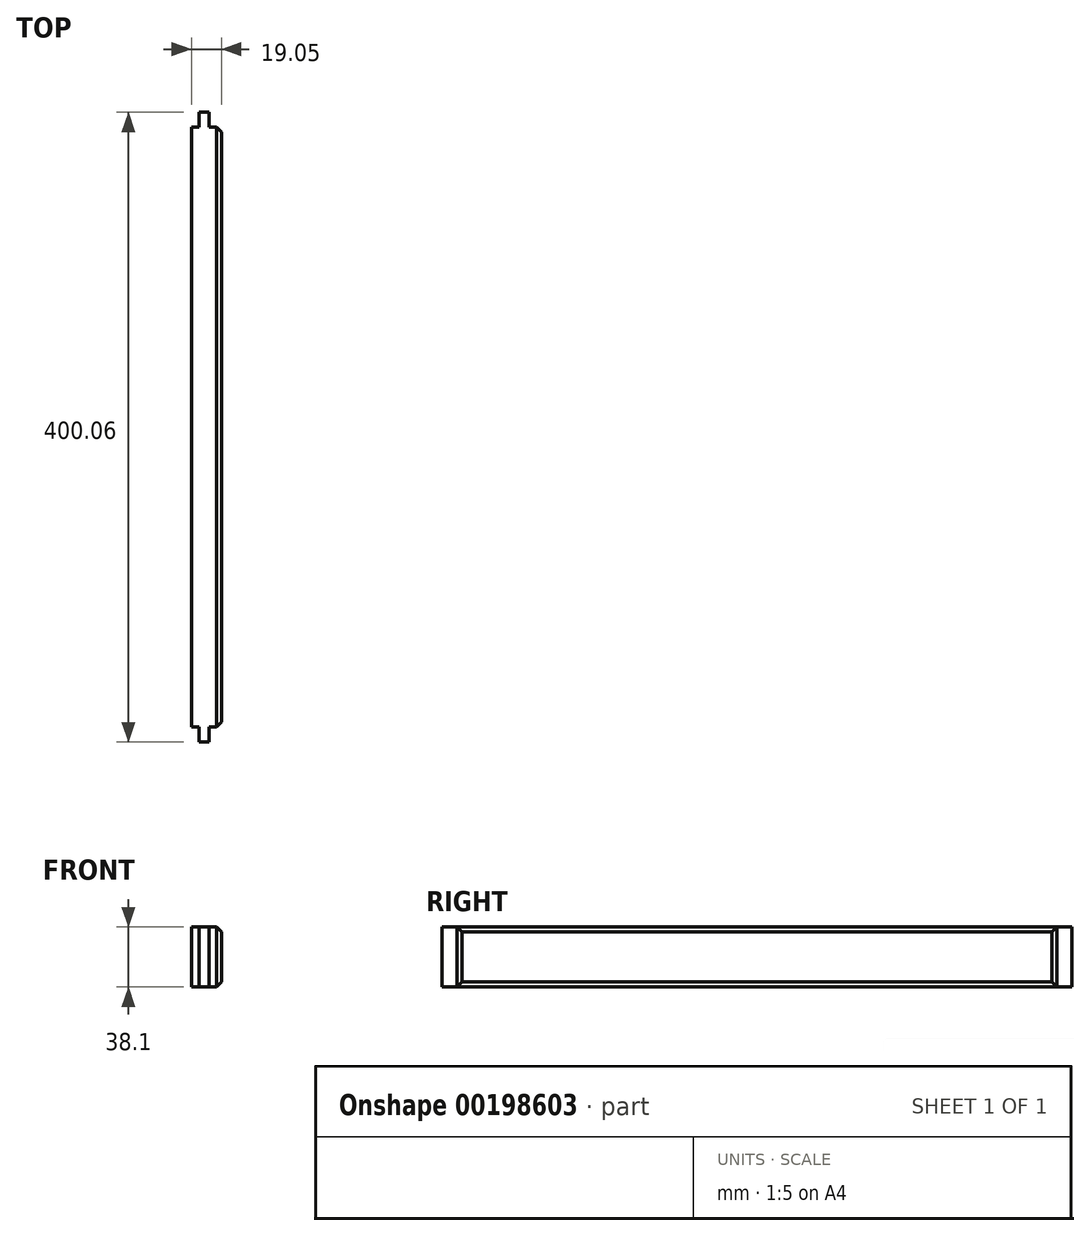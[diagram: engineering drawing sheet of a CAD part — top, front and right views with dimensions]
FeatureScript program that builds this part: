
annotation { "Feature Type Name" : "Feature", "Feature Type Description" : "" }
export const myFeature = defineFeature(function(context is Context, id is Id, definition is map)
    precondition{}
    {
        {
            var Q0;
            Q0=qCreatedBy(makeId("Front.planeOp"),FACE);
            var sketch = newSketch(context, id + "F0", { "sketchPlane" : qUnion([Q0])});
            skLineSegment(sketch, "E0.bottom", {"start": v(0, 0) * mm, "end": v(19.05, 0) * mm});
            skLineSegment(sketch, "E0.top", {"start": v(0, 38.1) * mm, "end": v(19.05, 38.1) * mm});
            skLineSegment(sketch, "E0.left", {"start": v(0, 0) * mm, "end": v(0, 38.1) * mm});
            skLineSegment(sketch, "E0.right", {"start": v(19.05, 0) * mm, "end": v(19.05, 38.1) * mm});
            skSolve(sketch);
        }
        {
            var Q0;
            Q0 = qSketchRegion(id + "F0", true);
            extrude(context, id + "F1", {"entities" : qUnion([Q0]), "depth" : 381 * mm});
        }
        {
            var Q0;
            Q0=makeQuery(id+"F1.opExtrude","SWEPT_EDGE",EDGE,{"disambiguationData":[OSD([sQuery(id+"F0.wireOp",EDGE,"E0.top"),sQuery(id+"F0.wireOp",EDGE,"E0.right")])]});
            var Q1;
            Q1=makeQuery(id+"F1.opExtrude","CAP_EDGE",EDGE,{"disambiguationData":[OSD([sQuery(id+"F0.wireOp",EDGE,"E0.right")])],"isStart":false});
            var Q2;
            Q2=makeQuery(id+"F1.opExtrude","CAP_EDGE",EDGE,{"disambiguationData":[OSD([sQuery(id+"F0.wireOp",EDGE,"E0.right")])],"isStart":true});
            var Q3;
            Q3=makeQuery(id+"F1.opExtrude","SWEPT_EDGE",EDGE,{"disambiguationData":[OSD([sQuery(id+"F0.wireOp",EDGE,"E0.bottom"),sQuery(id+"F0.wireOp",EDGE,"E0.right")])]});
            chamfer(context, id + "F2", {"entities" : qUnion([Q0, Q1, Q2, Q3]), "width" : 3.17 * mm, "tangentPropagation" : true});
        }
        {
            var Q0;
            Q0=makeQuery(id+"F1.opExtrude","CAP_FACE",FACE,{"disambiguationData":[OSD([sQuery(id+"F0.wireOp",EDGE,"E0.bottom"),sQuery(id+"F0.wireOp",EDGE,"E0.top"),sQuery(id+"F0.wireOp",EDGE,"E0.left"),sQuery(id+"F0.wireOp",EDGE,"E0.right")])],"isStart":false});
            var sketch = newSketch(context, id + "F3", { "sketchPlane" : qUnion([Q0])});
            skPoint(sketch, "E1.endSnap0", {"position": v(7.94, 0) * mm});
            skLineSegment(sketch, "E2", {"start": v(0, 38.1) * mm, "end": v(4.76, 38.1) * mm});
            skLineSegment(sketch, "E3.bottom", {"start": v(4.76, 38.1) * mm, "end": v(11.11, 38.1) * mm});
            skLineSegment(sketch, "E3.top", {"start": v(4.76, 0) * mm, "end": v(11.11, 0) * mm});
            skLineSegment(sketch, "E3.left", {"start": v(4.76, 38.1) * mm, "end": v(4.76, 0) * mm});
            skLineSegment(sketch, "E3.right", {"start": v(11.11, 38.1) * mm, "end": v(11.11, 0) * mm});
            skSolve(sketch);
        }
        {
            var Q0;
            Q0 = qSketchRegion(id + "F3", true);
            extrude(context, id + "F4", {"entities" : qUnion([Q0]), "operationType" : NewBodyOperationType.ADD, "depth" : 9.52 * mm});
        }
        {
            var Q0;
            Q0=makeQuery(id+"F1.opExtrude","CAP_FACE",FACE,{"disambiguationData":[OSD([sQuery(id+"F0.wireOp",EDGE,"E0.bottom"),sQuery(id+"F0.wireOp",EDGE,"E0.top"),sQuery(id+"F0.wireOp",EDGE,"E0.left"),sQuery(id+"F0.wireOp",EDGE,"E0.right")])],"isStart":true});
            var sketch = newSketch(context, id + "F5", { "sketchPlane" : qUnion([Q0])});
            skLineSegment(sketch, "E4", {"start": v(0, 38.1) * mm, "end": v(-4.76, 38.1) * mm});
            skLineSegment(sketch, "E5.bottom", {"start": v(-4.76, 38.1) * mm, "end": v(-11.11, 38.1) * mm});
            skLineSegment(sketch, "E5.top", {"start": v(-4.76, 0) * mm, "end": v(-11.11, 0) * mm});
            skLineSegment(sketch, "E5.left", {"start": v(-4.76, 38.1) * mm, "end": v(-4.76, 0) * mm});
            skLineSegment(sketch, "E5.right", {"start": v(-11.11, 38.1) * mm, "end": v(-11.11, 0) * mm});
            skSolve(sketch);
        }
        {
            var Q0;
            Q0 = qSketchRegion(id + "F5", true);
            extrude(context, id + "F6", {"entities" : qUnion([Q0]), "operationType" : NewBodyOperationType.ADD, "depth" : 9.52 * mm});
        }
    });
